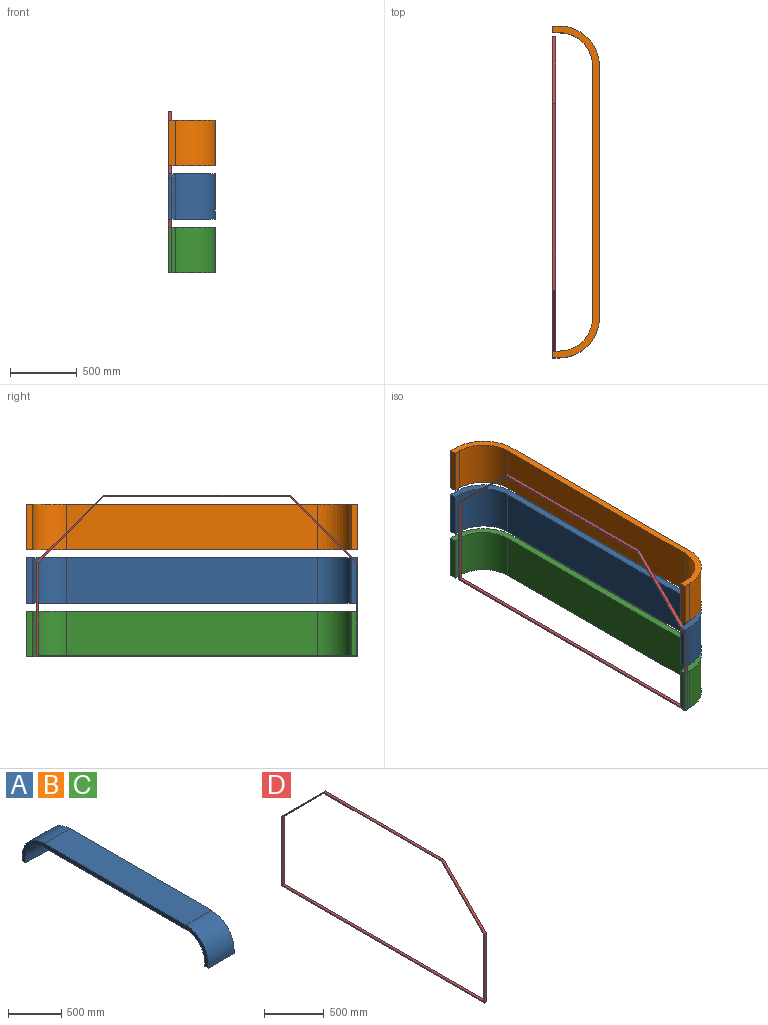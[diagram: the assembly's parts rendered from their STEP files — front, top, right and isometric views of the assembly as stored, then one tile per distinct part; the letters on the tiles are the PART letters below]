
ASSEMBLY  parts=4 mates=1
PART A: 14 faces, bbox 340x2480x350 mm
  f0: plane 340x50mm, normal (0,-1,0), area 17000mm2, adj f1,f11,f12,f13
  f1: plane 340x50mm, normal (0,0,-1), area 17000mm2, adj f0,f2,f12,f13
  f2: plane 340x50mm, normal (0,1,0), area 17000mm2, adj f1,f3,f12,f13
  f3: cylinder r=300mm len=340mm, axis (-1,0,0), area 160221.2mm2, adj f2,f4,f12,f13
  f4: plane 1880x340mm, normal (0,0,1), area 639200mm2, adj f3,f5,f12,f13
  f5: cylinder r=300mm len=340mm, axis (-1,0,0), area 160221.2mm2, adj f4,f6,f12,f13
  f6: plane 340x50mm, normal (0,-1,0), area 17000mm2, adj f5,f7,f12,f13
  f7: plane 340x50mm, normal (0,0,-1), area 17000mm2, adj f6,f8,f12,f13
  f8: plane 340x50mm, normal (0,1,0), area 17000mm2, adj f7,f9,f12,f13
  f9: cylinder r=250mm len=340mm, axis (-1,0,0), area 133517.7mm2, adj f8,f10,f12,f13
  f10: plane 1880x340mm, normal (0,0,-1), area 639200mm2, adj f9,f11,f12,f13
  f11: cylinder r=250mm len=340mm, axis (-1,0,0), area 133517.7mm2, adj f0,f10,f12,f13
  f12: plane 2480x350mm, normal (1,0,0), area 142196.9mm2, adj f0,f1,f2,f3,f4,f5,f6,f7
  f13: plane 2480x350mm, normal (-1,0,0), area 142196.9mm2, adj f0,f1,f2,f3,f4,f5,f6,f7
PART B: same geometry as A
PART C: same geometry as A
PART D: 14 faces, bbox 25x2400x1205 mm
  f0: plane 1397.07x25mm, normal (0,0,1), area 34926.8mm2, adj f1,f11,f12,f13
  f1: plane 505x505mm, normal (0,-0.71,0.71), area 17854.4mm2, adj f0,f2,f12,f13
  f2: plane 700x25mm, normal (0,-1,0), area 17500mm2, adj f1,f3,f12,f13
  f3: plane 2400x25mm, normal (0,0,-1), area 60000mm2, adj f2,f4,f12,f13
  f4: plane 707.07x25mm, normal (0,1,0), area 17676.8mm2, adj f3,f11,f12,f13
  f5: plane 2380x25mm, normal (0,0,1), area 59500mm2, adj f6,f10,f12,f13
  f6: plane 685.86x25mm, normal (0,1,0), area 17146.4mm2, adj f5,f7,f12,f13
  f7: plane 499.14x499.14mm, normal (0,0.71,-0.71), area 17647.3mm2, adj f6,f8,f12,f13
  f8: plane 1388.79x25mm, normal (0,0,-1), area 34719.7mm2, adj f7,f9,f12,f13
  f9: plane 492.07x492.07mm, normal (0,-0.71,-0.71), area 17397.3mm2, adj f8,f10,f12,f13
  f10: plane 692.93x25mm, normal (0,-1,0), area 17323.2mm2, adj f5,f9,f12,f13
  f11: plane 497.93x497.93mm, normal (0,0.71,0.71), area 17604.4mm2, adj f0,f4,f12,f13
  f12: plane 2400x1205mm, normal (1,0,0), area 65859.3mm2, adj f0,f1,f2,f3,f4,f5,f6,f7
  f13: plane 2400x1205mm, normal (-1,0,0), area 65859.3mm2, adj f0,f1,f2,f3,f4,f5,f6,f7
PLACE A rot(axis=(0,1,0),90deg) t=(-12.5,0,570)mm
PLACE B rot(axis=(0,1,0),90deg) t=(-12.5,0,970)mm
PLACE C rot(axis=(0,1,0),90deg) t=(-12.5,0,170)mm
PLACE D at identity fixed
MATE fastened D.f13 <-> C.f7  axis (-1,0,0) through (-12.5,0,0)mm
